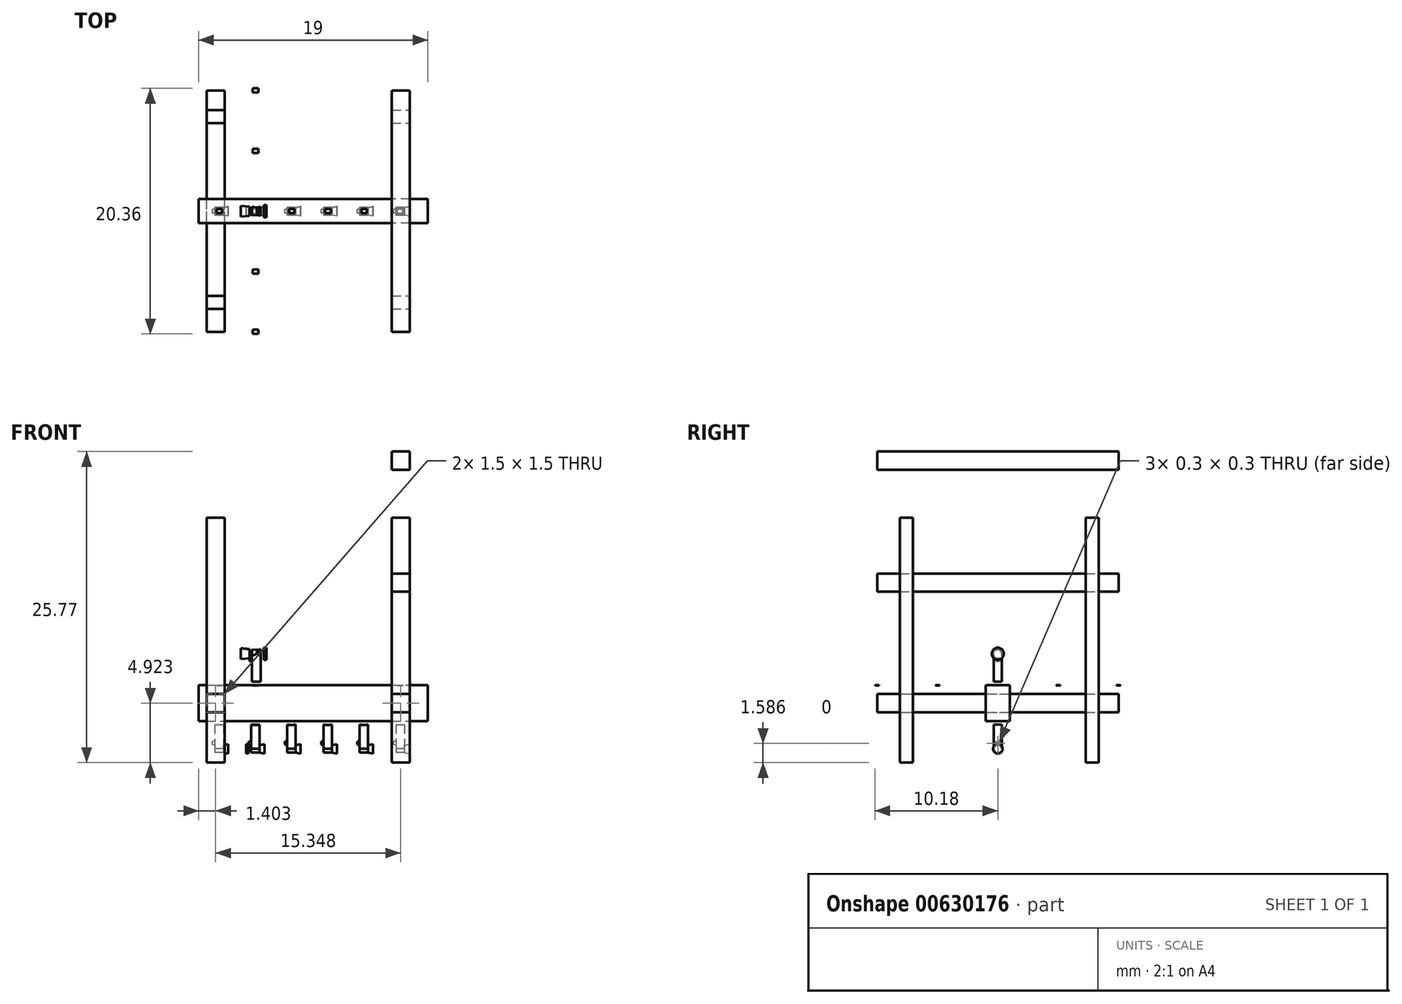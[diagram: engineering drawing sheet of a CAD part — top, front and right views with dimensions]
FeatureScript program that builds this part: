
annotation { "Feature Type Name" : "Feature", "Feature Type Description" : "" }
export const myFeature = defineFeature(function(context is Context, id is Id, definition is map)
    precondition{}
    {
        {
            var Q0;
            Q0=qCreatedBy(makeId("Front.planeOp"),FACE);
            var sketch = newSketch(context, id + "F0", { "sketchPlane" : qUnion([Q0])});
            skLineSegment(sketch, "E0.bottom", {"start": v(-0.48, 0) * mm, "end": v(0.22, 0) * mm});
            skLineSegment(sketch, "E0.top", {"start": v(-0.48, -2) * mm, "end": v(0.22, -2) * mm});
            skLineSegment(sketch, "E0.left", {"start": v(-0.48, 0) * mm, "end": v(-0.48, -2) * mm});
            skLineSegment(sketch, "E0.right", {"start": v(0.22, 0) * mm, "end": v(0.22, -2) * mm});
            skLineSegment(sketch, "E1.bottom", {"start": v(-0.48, 0) * mm, "end": v(-0.68, 0) * mm});
            skLineSegment(sketch, "E1.top", {"start": v(-0.48, -0.3) * mm, "end": v(-0.68, -0.3) * mm});
            skLineSegment(sketch, "E1.left", {"start": v(-0.48, 0) * mm, "end": v(-0.48, -0.3) * mm});
            skLineSegment(sketch, "E1.right", {"start": v(-0.68, 0) * mm, "end": v(-0.68, -0.3) * mm});
            skLineSegment(sketch, "E2", {"start": v(-0.1, 0) * mm, "end": v(-1.4, -0.13) * mm});
            skLineSegment(sketch, "E3", {"start": v(-1.4, -0.13) * mm, "end": v(-1.4, 0.32) * mm});
            skLineSegment(sketch, "E4", {"start": v(-1.4, 0.32) * mm, "end": v(0, 0.32) * mm});
            skLineSegment(sketch, "E5", {"start": v(0, 0.32) * mm, "end": v(0, 0) * mm});
            skLineSegment(sketch, "E6", {"start": v(0, 0) * mm, "end": v(0.5, -0.13) * mm});
            skLineSegment(sketch, "E7", {"start": v(0.5, -0.13) * mm, "end": v(0.5, 0.32) * mm});
            skLineSegment(sketch, "E8", {"start": v(0, 0.32) * mm, "end": v(0.5, 0.32) * mm});
            skLineSegment(sketch, "E9.bottom", {"start": v(0.5, 0.32) * mm, "end": v(0.7, 0.32) * mm});
            skLineSegment(sketch, "E9.top", {"start": v(0.5, -0.18) * mm, "end": v(0.7, -0.18) * mm});
            skLineSegment(sketch, "E9.left", {"start": v(0.5, 0.32) * mm, "end": v(0.5, -0.18) * mm});
            skLineSegment(sketch, "E9.right", {"start": v(0.7, 0.32) * mm, "end": v(0.7, -0.18) * mm});
            skLineSegment(sketch, "E10.bottom", {"start": v(-0.42, -2) * mm, "end": v(0.03, -2) * mm});
            skLineSegment(sketch, "E10.top", {"start": v(-0.42, -2.3) * mm, "end": v(0.03, -2.3) * mm});
            skLineSegment(sketch, "E10.left", {"start": v(-0.42, -2) * mm, "end": v(-0.42, -2.3) * mm});
            skLineSegment(sketch, "E10.right", {"start": v(0.03, -2) * mm, "end": v(0.03, -2.3) * mm});
            skLineSegment(sketch, "E11.top", {"start": v(-0.48, 0.32) * mm, "end": v(0.22, 0.32) * mm});
            skLineSegment(sketch, "E11.left", {"start": v(-0.48, 0) * mm, "end": v(-0.48, 0.32) * mm});
            skLineSegment(sketch, "E11.right", {"start": v(0.22, 0) * mm, "end": v(0.22, 0.32) * mm});
            skLineSegment(sketch, "E12.bottom", {"start": v(-0.68, 0) * mm, "end": v(-0.48, 0) * mm});
            skLineSegment(sketch, "E12.top", {"start": v(-0.68, 0.32) * mm, "end": v(-0.48, 0.32) * mm});
            skLineSegment(sketch, "E12.left", {"start": v(-0.68, 0) * mm, "end": v(-0.68, 0.32) * mm});
            skLineSegment(sketch, "E13.bottom", {"start": v(-4.9, -2.28) * mm, "end": v(14.1, -2.28) * mm});
            skLineSegment(sketch, "E13.top", {"start": v(-4.9, -5.28) * mm, "end": v(14.1, -5.28) * mm});
            skLineSegment(sketch, "E13.left", {"start": v(-4.9, -2.28) * mm, "end": v(-4.9, -5.28) * mm});
            skLineSegment(sketch, "E13.right", {"start": v(14.1, -2.28) * mm, "end": v(14.1, -5.28) * mm});
            skLineSegment(sketch, "E14.bottom", {"start": v(0, -5.28) * mm, "end": v(-0.45, -5.28) * mm});
            skLineSegment(sketch, "E14.top", {"start": v(0, -5.58) * mm, "end": v(-0.45, -5.58) * mm});
            skLineSegment(sketch, "E14.left", {"start": v(0, -5.28) * mm, "end": v(0, -5.58) * mm});
            skLineSegment(sketch, "E14.right", {"start": v(-0.45, -5.28) * mm, "end": v(-0.45, -5.58) * mm});
            skLineSegment(sketch, "E15.bottom", {"start": v(-0.56, -5.56) * mm, "end": v(0.14, -5.56) * mm});
            skLineSegment(sketch, "E15.top", {"start": v(-0.56, -7.56) * mm, "end": v(0.14, -7.56) * mm});
            skLineSegment(sketch, "E15.left", {"start": v(-0.56, -5.56) * mm, "end": v(-0.56, -7.56) * mm});
            skLineSegment(sketch, "E15.right", {"start": v(0.14, -5.56) * mm, "end": v(0.14, -7.56) * mm});
            skLineSegment(sketch, "E16", {"start": v(0.14, -7.56) * mm, "end": v(0.54, -7.56) * mm});
            skLineSegment(sketch, "E17", {"start": v(0.54, -7.56) * mm, "end": v(0.54, -7.16) * mm});
            skLineSegment(sketch, "E18", {"start": v(0.54, -7.16) * mm, "end": v(0.14, -7.26) * mm});
            skLineSegment(sketch, "E19", {"start": v(0.14, -7.26) * mm, "end": v(0.14, -7.56) * mm});
            skLineSegment(sketch, "E20", {"start": v(0.14, -7.26) * mm, "end": v(-0.56, -7.26) * mm});
            skLineSegment(sketch, "E21", {"start": v(-0.56, -7.26) * mm, "end": v(-0.96, -7.16) * mm});
            skLineSegment(sketch, "E22", {"start": v(-0.96, -7.56) * mm, "end": v(-0.96, -7.16) * mm});
            skLineSegment(sketch, "E23", {"start": v(-0.96, -7.56) * mm, "end": v(-0.56, -7.56) * mm});
            skLineSegment(sketch, "E24.bottom", {"start": v(-0.56, -7.56) * mm, "end": v(-0.76, -7.56) * mm});
            skLineSegment(sketch, "E24.top", {"start": v(-0.56, -6.96) * mm, "end": v(-0.76, -6.96) * mm});
            skLineSegment(sketch, "E24.left", {"start": v(-0.56, -7.56) * mm, "end": v(-0.56, -6.96) * mm});
            skLineSegment(sketch, "E24.right", {"start": v(-0.76, -7.56) * mm, "end": v(-0.76, -6.96) * mm});
            skLineSegment(sketch, "E25.bottom", {"start": v(-4.26, -3.03) * mm, "end": v(-2.76, -3.03) * mm});
            skLineSegment(sketch, "E25.top", {"start": v(-4.26, -4.53) * mm, "end": v(-2.76, -4.53) * mm});
            skLineSegment(sketch, "E25.left", {"start": v(-4.26, -3.03) * mm, "end": v(-4.26, -4.53) * mm});
            skLineSegment(sketch, "E25.right", {"start": v(-2.76, -3.03) * mm, "end": v(-2.76, -4.53) * mm});
            skLineSegment(sketch, "E26.bottom", {"start": v(12.6, -3.03) * mm, "end": v(11.1, -3.03) * mm});
            skLineSegment(sketch, "E26.top", {"start": v(12.6, -4.53) * mm, "end": v(11.1, -4.53) * mm});
            skLineSegment(sketch, "E26.left", {"start": v(12.6, -3.03) * mm, "end": v(12.6, -4.53) * mm});
            skLineSegment(sketch, "E26.right", {"start": v(11.1, -3.03) * mm, "end": v(11.1, -4.53) * mm});
            skLineSegment(sketch, "E27", {"start": v(-4.26, -3.03) * mm, "end": v(-4.26, -2.28) * mm});
            skLineSegment(sketch, "E28", {"start": v(12.6, -3.03) * mm, "end": v(12.6, -2.28) * mm});
            skSolve(sketch);
        }
        {
            var Q0;
            Q0=makeQuery(id+"F0.imprint","IMPRINT",FACE,{"disambiguationData":[TD([[makeQuery(id+"F0.imprint","IMPRINT",EDGE,{"derivedFrom":sQuery(id+"F0.wireOp",EDGE,"E12.bottom")}),1.0]])]});
            var Q1;
            {var subQ0=sQuery(id+"F0.wireOp",EDGE,"E12.bottom");Q1=makeQuery(id+"F0.imprint","IMPRINT",FACE,{"disambiguationData":[TD([[makeQuery(id+"F0.imprint","IMPRINT",EDGE,{"derivedFrom":subQ0}),-1.0]])]});}
            var Q2;
            {var subQ0=sQuery(id+"F0.wireOp",EDGE,"E0.bottom");var subQ3=sQuery(id+"F0.wireOp",EDGE,"E2");var subQ5=makeQuery(id+"F0.imprint","INTERSECT",VERTEX,{"derivedFrom":[subQ3,subQ0]});Q2=makeQuery(id+"F0.imprint","IMPRINT",FACE,{"disambiguationData":[TD([[makeQuery(id+"F0.imprint","IMPRINT",EDGE,{"disambiguationData":[TD([[subQ5,-1.0]])],"derivedFrom":subQ3}),-1.0]])]});}
            var Q3;
            {var subQ1=sQuery(id+"F0.wireOp",EDGE,"E5");Q3=makeQuery(id+"F0.imprint","IMPRINT",FACE,{"disambiguationData":[TD([[makeQuery(id+"F0.imprint","IMPRINT",EDGE,{"derivedFrom":subQ1}),-1.0]])]});}
            var Q4;
            {var subQ0=sQuery(id+"F0.wireOp",EDGE,"E5");Q4=makeQuery(id+"F0.imprint","IMPRINT",FACE,{"disambiguationData":[TD([[makeQuery(id+"F0.imprint","IMPRINT",EDGE,{"derivedFrom":subQ0}),1.0]])]});}
            var Q5;
            {var subQ1=sQuery(id+"F0.wireOp",EDGE,"E0.right");var subQ3=sQuery(id+"F0.wireOp",EDGE,"E6");var subQ4=makeQuery(id+"F0.imprint","INTERSECT",VERTEX,{"derivedFrom":[subQ1,subQ3]});Q5=makeQuery(id+"F0.imprint","IMPRINT",FACE,{"disambiguationData":[TD([[makeQuery(id+"F0.imprint","IMPRINT",EDGE,{"disambiguationData":[TD([[subQ4,1.0]])],"derivedFrom":subQ1}),-1.0]])]});}
            var Q6;
            {var subQ3=sQuery(id+"F0.wireOp",EDGE,"E9.bottom");Q6=makeQuery(id+"F0.imprint","IMPRINT",FACE,{"disambiguationData":[TD([[makeQuery(id+"F0.imprint","IMPRINT",EDGE,{"derivedFrom":subQ3}),-1.0]])]});}
            var Q7;
            {var subQ3=sQuery(id+"F0.wireOp",EDGE,"E8");Q7=makeQuery(id+"F0.imprint","IMPRINT",FACE,{"disambiguationData":[TD([[makeQuery(id+"F0.imprint","IMPRINT",EDGE,{"derivedFrom":subQ3}),-1.0]])]});}
            var Q8;
            {var subQ1=sQuery(id+"F0.wireOp",EDGE,"E3");Q8=makeQuery(id+"F0.imprint","IMPRINT",FACE,{"disambiguationData":[TD([[makeQuery(id+"F0.imprint","IMPRINT",EDGE,{"derivedFrom":subQ1}),-1.0]])]});}
            var Q9;
            Q9=sQuery(id+"F0.wireOp",EDGE,"E4");
            revolve(context, id + "F1", {"entities" : qUnion([Q0, Q1, Q2, Q3, Q4, Q5, Q6, Q7, Q8]), "axis" : qUnion([Q9]), "revolveType" : RevolveType.FULL});
        }
        {
            var Q0;
            {var subQ0=sQuery(id+"F0.wireOp",EDGE,"E1.top");Q0=makeQuery(id+"F0.imprint","IMPRINT",FACE,{"disambiguationData":[TD([[makeQuery(id+"F0.imprint","IMPRINT",EDGE,{"derivedFrom":subQ0}),-1.0]])]});}
            var Q1;
            Q1=makeQuery(id+"F0.imprint","IMPRINT",FACE,{"disambiguationData":[TD([[makeQuery(id+"F0.imprint","IMPRINT",EDGE,{"derivedFrom":sQuery(id+"F0.wireOp",EDGE,"E12.bottom")}),1.0]])]});
            var Q2;
            {var subQ0=sQuery(id+"F0.wireOp",EDGE,"E12.bottom");Q2=makeQuery(id+"F0.imprint","IMPRINT",FACE,{"disambiguationData":[TD([[makeQuery(id+"F0.imprint","IMPRINT",EDGE,{"derivedFrom":subQ0}),-1.0]])]});}
            extrude(context, id + "F2", {"entities" : qUnion([Q0, Q1, Q2]), "operationType" : NewBodyOperationType.ADD, "depth" : 0.3 * mm, "offsetDistance" : 25 * mm, "symmetric" : true});
        }
        {
            var Q0;
            {var subQ5=sQuery(id+"F0.wireOp",EDGE,"E0.left");Q0=makeQuery(id+"F0.imprint","IMPRINT",FACE,{"disambiguationData":[TD([[makeQuery(id+"F0.imprint","IMPRINT",EDGE,{"derivedFrom":subQ5}),1.0]])]});}
            var Q1;
            {var subQ0=sQuery(id+"F0.wireOp",EDGE,"E0.bottom");var subQ3=sQuery(id+"F0.wireOp",EDGE,"E2");var subQ5=makeQuery(id+"F0.imprint","INTERSECT",VERTEX,{"derivedFrom":[subQ3,subQ0]});Q1=makeQuery(id+"F0.imprint","IMPRINT",FACE,{"disambiguationData":[TD([[makeQuery(id+"F0.imprint","IMPRINT",EDGE,{"disambiguationData":[TD([[subQ5,-1.0]])],"derivedFrom":subQ3}),-1.0]])]});}
            var Q2;
            {var subQ1=sQuery(id+"F0.wireOp",EDGE,"E0.right");var subQ3=sQuery(id+"F0.wireOp",EDGE,"E6");var subQ4=makeQuery(id+"F0.imprint","INTERSECT",VERTEX,{"derivedFrom":[subQ1,subQ3]});Q2=makeQuery(id+"F0.imprint","IMPRINT",FACE,{"disambiguationData":[TD([[makeQuery(id+"F0.imprint","IMPRINT",EDGE,{"disambiguationData":[TD([[subQ4,1.0]])],"derivedFrom":subQ1}),-1.0]])]});}
            var Q3;
            {var subQ1=sQuery(id+"F0.wireOp",EDGE,"E5");Q3=makeQuery(id+"F0.imprint","IMPRINT",FACE,{"disambiguationData":[TD([[makeQuery(id+"F0.imprint","IMPRINT",EDGE,{"derivedFrom":subQ1}),-1.0]])]});}
            var Q4;
            {var subQ0=sQuery(id+"F0.wireOp",EDGE,"E5");Q4=makeQuery(id+"F0.imprint","IMPRINT",FACE,{"disambiguationData":[TD([[makeQuery(id+"F0.imprint","IMPRINT",EDGE,{"derivedFrom":subQ0}),1.0]])]});}
            extrude(context, id + "F3", {"entities" : qUnion([Q0, Q1, Q2, Q3, Q4]), "operationType" : NewBodyOperationType.ADD, "depth" : 0.65 * mm, "offsetDistance" : 25 * mm, "symmetric" : true});
        }
        {
            var Q0;
            Q0=makeQuery(id+"F0.imprint","IMPRINT",FACE,{"disambiguationData":[TD([[makeQuery(id+"F0.imprint","IMPRINT",EDGE,{"derivedFrom":sQuery(id+"F0.wireOp",EDGE,"E16")}),1.0]])]});
            var Q1;
            {var subQ5=sQuery(id+"F0.wireOp",EDGE,"E24.bottom");Q1=makeQuery(id+"F0.imprint","IMPRINT",FACE,{"disambiguationData":[TD([[makeQuery(id+"F0.imprint","IMPRINT",EDGE,{"derivedFrom":subQ5}),-1.0]])]});}
            var Q2;
            {var subQ0=sQuery(id+"F0.wireOp",EDGE,"E22");Q2=makeQuery(id+"F0.imprint","IMPRINT",FACE,{"disambiguationData":[TD([[makeQuery(id+"F0.imprint","IMPRINT",EDGE,{"derivedFrom":subQ0}),-1.0]])]});}
            var Q3;
            {var subQ0=sQuery(id+"F0.wireOp",EDGE,"E15.top");Q3=makeQuery(id+"F0.imprint","IMPRINT",FACE,{"disambiguationData":[TD([[makeQuery(id+"F0.imprint","IMPRINT",EDGE,{"derivedFrom":subQ0}),1.0]])]});}
            var Q4;
            Q4=sQuery(id+"F0.wireOp",EDGE,"E16");
            revolve(context, id + "F4", {"entities" : qUnion([Q0, Q1, Q2, Q3]), "axis" : qUnion([Q4]), "revolveType" : RevolveType.FULL});
        }
        {
            var Q0;
            {var subQ1=sQuery(id+"F0.wireOp",EDGE,"E14.top");Q0=makeQuery(id+"F0.imprint","IMPRINT",FACE,{"disambiguationData":[TD([[makeQuery(id+"F0.imprint","IMPRINT",EDGE,{"derivedFrom":subQ1}),1.0]])]});}
            var Q1;
            {var subQ0=sQuery(id+"F0.wireOp",EDGE,"E15.top");Q1=makeQuery(id+"F0.imprint","IMPRINT",FACE,{"disambiguationData":[TD([[makeQuery(id+"F0.imprint","IMPRINT",EDGE,{"derivedFrom":subQ0}),1.0]])]});}
            extrude(context, id + "F5", {"entities" : qUnion([Q0, Q1]), "operationType" : NewBodyOperationType.ADD, "depth" : 0.65 * mm, "offsetDistance" : 25 * mm, "symmetric" : true});
        }
        {
            var Q0;
            {var subQ5=sQuery(id+"F0.wireOp",EDGE,"E24.top");Q0=makeQuery(id+"F0.imprint","IMPRINT",FACE,{"disambiguationData":[TD([[makeQuery(id+"F0.imprint","IMPRINT",EDGE,{"derivedFrom":subQ5}),1.0]])]});}
            var Q1;
            {var subQ5=sQuery(id+"F0.wireOp",EDGE,"E24.bottom");Q1=makeQuery(id+"F0.imprint","IMPRINT",FACE,{"disambiguationData":[TD([[makeQuery(id+"F0.imprint","IMPRINT",EDGE,{"derivedFrom":subQ5}),-1.0]])]});}
            extrude(context, id + "F6", {"entities" : qUnion([Q0, Q1]), "operationType" : NewBodyOperationType.ADD, "depth" : 0.3 * mm, "offsetDistance" : 25 * mm, "symmetric" : true});
        }
        {
            var Q0;
            {var subQ0=sQuery(id+"F0.wireOp",EDGE,"E14.bottom");Q0=makeQuery(id+"F0.imprint","IMPRINT",FACE,{"disambiguationData":[TD([[makeQuery(id+"F0.imprint","IMPRINT",EDGE,{"derivedFrom":subQ0}),1.0]])]});}
            var Q1;
            {var subQ0=sQuery(id+"F0.wireOp",EDGE,"E14.top");Q1=makeQuery(id+"F0.imprint","IMPRINT",FACE,{"disambiguationData":[TD([[makeQuery(id+"F0.imprint","IMPRINT",EDGE,{"derivedFrom":subQ0}),-1.0]])]});}
            extrude(context, id + "F7", {"entities" : qUnion([Q0, Q1]), "depth" : 0.35 * mm, "offsetDistance" : 25 * mm, "symmetric" : true});
        }
        {
            var Q0;
            {var subQ0=sQuery(id+"F0.wireOp",EDGE,"E10.bottom");Q0=makeQuery(id+"F0.imprint","IMPRINT",FACE,{"disambiguationData":[TD([[makeQuery(id+"F0.imprint","IMPRINT",EDGE,{"derivedFrom":subQ0}),-1.0]])]});}
            var Q1;
            {var subQ0=sQuery(id+"F0.wireOp",EDGE,"E10.top");Q1=makeQuery(id+"F0.imprint","IMPRINT",FACE,{"disambiguationData":[TD([[makeQuery(id+"F0.imprint","IMPRINT",EDGE,{"derivedFrom":subQ0}),1.0]])]});}
            extrude(context, id + "F8", {"entities" : qUnion([Q0, Q1]), "depth" : 0.35 * mm, "offsetDistance" : 25 * mm, "symmetric" : true});
        }
        {
            var Q0;
            {var subQ1=sQuery(id+"F0.wireOp",EDGE,"E10.top");Q0=makeQuery(id+"F0.imprint","IMPRINT",FACE,{"disambiguationData":[TD([[makeQuery(id+"F0.imprint","IMPRINT",EDGE,{"derivedFrom":subQ1}),-1.0]])]});}
            var Q1;
            {var subQ0=sQuery(id+"F0.wireOp",EDGE,"E10.top");Q1=makeQuery(id+"F0.imprint","IMPRINT",FACE,{"disambiguationData":[TD([[makeQuery(id+"F0.imprint","IMPRINT",EDGE,{"derivedFrom":subQ0}),1.0]])]});}
            extrude(context, id + "F9", {"entities" : qUnion([Q0, Q1]), "depth" : 2 * mm, "offsetDistance" : 25 * mm, "symmetric" : true});
        }
        {
            var Q0;
            Q0=makeQuery(id+"F4.opRevolve","SWEPT_BODY",BODY,{"disambiguationData":[OSD([sQuery(id+"F0.wireOp",EDGE,"E15.top"),sQuery(id+"F0.wireOp",EDGE,"E16"),sQuery(id+"F0.wireOp",EDGE,"E17"),sQuery(id+"F0.wireOp",EDGE,"E18"),sQuery(id+"F0.wireOp",EDGE,"E20"),sQuery(id+"F0.wireOp",EDGE,"E21"),sQuery(id+"F0.wireOp",EDGE,"E22"),sQuery(id+"F0.wireOp",EDGE,"E23"),sQuery(id+"F0.wireOp",EDGE,"E24.bottom")])]});
            transform(context, id + "F10", {"entities" : qUnion([Q0]), "transformType" : TransformType.TRANSLATION_3D, "dx" : 3 * mm, "dy" : 0 * mm, "dz" : 0 * mm, "makeCopy" : true});
        }
        {
            var Q0;
            Q0=makeQuery(id+"F4.opRevolve","SWEPT_BODY",BODY,{"disambiguationData":[OSD([sQuery(id+"F0.wireOp",EDGE,"E15.top"),sQuery(id+"F0.wireOp",EDGE,"E16"),sQuery(id+"F0.wireOp",EDGE,"E17"),sQuery(id+"F0.wireOp",EDGE,"E18"),sQuery(id+"F0.wireOp",EDGE,"E20"),sQuery(id+"F0.wireOp",EDGE,"E21"),sQuery(id+"F0.wireOp",EDGE,"E22"),sQuery(id+"F0.wireOp",EDGE,"E23"),sQuery(id+"F0.wireOp",EDGE,"E24.bottom")])]});
            transform(context, id + "F11", {"entities" : qUnion([Q0]), "transformType" : TransformType.TRANSLATION_3D, "dx" : -3 * mm, "dy" : 0 * mm, "dz" : 0 * mm, "makeCopy" : true});
        }
        {
            var Q0;
            Q0=makeQuery(id+"F8.opExtrude","SWEPT_BODY",BODY,{"disambiguationData":[OSD([sQuery(id+"F0.wireOp",EDGE,"E10.bottom"),sQuery(id+"F0.wireOp",EDGE,"E10.top"),sQuery(id+"F0.wireOp",EDGE,"E10.left"),sQuery(id+"F0.wireOp",EDGE,"E10.right")])]});
            transform(context, id + "F12", {"entities" : qUnion([Q0]), "transformType" : TransformType.TRANSLATION_3D, "dx" : 3 * mm, "dy" : 0 * mm, "dz" : 0 * mm, "makeCopy" : true});
        }
        {
            var Q0;
            Q0=makeQuery(id+"F8.opExtrude","SWEPT_BODY",BODY,{"disambiguationData":[OSD([sQuery(id+"F0.wireOp",EDGE,"E10.bottom"),sQuery(id+"F0.wireOp",EDGE,"E10.top"),sQuery(id+"F0.wireOp",EDGE,"E10.left"),sQuery(id+"F0.wireOp",EDGE,"E10.right")])]});
            transform(context, id + "F13", {"entities" : qUnion([Q0]), "transformType" : TransformType.TRANSLATION_3D, "dx" : -3 * mm, "dy" : 0 * mm, "dz" : 0 * mm, "makeCopy" : true});
        }
        {
            var Q0;
            Q0=makeQuery(id+"F4.opRevolve","SWEPT_BODY",BODY,{"disambiguationData":[OSD([sQuery(id+"F0.wireOp",EDGE,"E15.top"),sQuery(id+"F0.wireOp",EDGE,"E16"),sQuery(id+"F0.wireOp",EDGE,"E17"),sQuery(id+"F0.wireOp",EDGE,"E18"),sQuery(id+"F0.wireOp",EDGE,"E20"),sQuery(id+"F0.wireOp",EDGE,"E21"),sQuery(id+"F0.wireOp",EDGE,"E22"),sQuery(id+"F0.wireOp",EDGE,"E23"),sQuery(id+"F0.wireOp",EDGE,"E24.bottom")])]});
            transform(context, id + "F14", {"entities" : qUnion([Q0]), "transformType" : TransformType.TRANSLATION_3D, "dx" : 6 * mm, "dy" : 0 * mm, "dz" : 0 * mm, "makeCopy" : true});
        }
        {
            var Q0;
            Q0=makeQuery(id+"F4.opRevolve","SWEPT_BODY",BODY,{"disambiguationData":[OSD([sQuery(id+"F0.wireOp",EDGE,"E15.top"),sQuery(id+"F0.wireOp",EDGE,"E16"),sQuery(id+"F0.wireOp",EDGE,"E17"),sQuery(id+"F0.wireOp",EDGE,"E18"),sQuery(id+"F0.wireOp",EDGE,"E20"),sQuery(id+"F0.wireOp",EDGE,"E21"),sQuery(id+"F0.wireOp",EDGE,"E22"),sQuery(id+"F0.wireOp",EDGE,"E23"),sQuery(id+"F0.wireOp",EDGE,"E24.bottom")])]});
            transform(context, id + "F15", {"entities" : qUnion([Q0]), "transformType" : TransformType.TRANSLATION_3D, "dx" : 9 * mm, "dy" : 0 * mm, "dz" : 0 * mm, "makeCopy" : true});
        }
        {
            var Q0;
            Q0=makeQuery(id+"F4.opRevolve","SWEPT_BODY",BODY,{"disambiguationData":[OSD([sQuery(id+"F0.wireOp",EDGE,"E15.top"),sQuery(id+"F0.wireOp",EDGE,"E16"),sQuery(id+"F0.wireOp",EDGE,"E17"),sQuery(id+"F0.wireOp",EDGE,"E18"),sQuery(id+"F0.wireOp",EDGE,"E20"),sQuery(id+"F0.wireOp",EDGE,"E21"),sQuery(id+"F0.wireOp",EDGE,"E22"),sQuery(id+"F0.wireOp",EDGE,"E23"),sQuery(id+"F0.wireOp",EDGE,"E24.bottom")])]});
            transform(context, id + "F16", {"entities" : qUnion([Q0]), "transformType" : TransformType.TRANSLATION_3D, "dx" : 12 * mm, "dy" : 0 * mm, "dz" : 0 * mm, "makeCopy" : true});
        }
        {
            var Q0;
            Q0=makeQuery(id+"F8.opExtrude","SWEPT_BODY",BODY,{"disambiguationData":[OSD([sQuery(id+"F0.wireOp",EDGE,"E10.bottom"),sQuery(id+"F0.wireOp",EDGE,"E10.top"),sQuery(id+"F0.wireOp",EDGE,"E10.left"),sQuery(id+"F0.wireOp",EDGE,"E10.right")])]});
            transform(context, id + "F17", {"entities" : qUnion([Q0]), "transformType" : TransformType.TRANSLATION_3D, "dx" : 6 * mm, "dy" : 0 * mm, "dz" : 0 * mm, "makeCopy" : true});
        }
        {
            var Q0;
            Q0=makeQuery(id+"F8.opExtrude","SWEPT_BODY",BODY,{"disambiguationData":[OSD([sQuery(id+"F0.wireOp",EDGE,"E10.bottom"),sQuery(id+"F0.wireOp",EDGE,"E10.top"),sQuery(id+"F0.wireOp",EDGE,"E10.left"),sQuery(id+"F0.wireOp",EDGE,"E10.right")])]});
            transform(context, id + "F18", {"entities" : qUnion([Q0]), "transformType" : TransformType.TRANSLATION_3D, "dx" : 12 * mm, "dy" : 0 * mm, "dz" : 0 * mm, "makeCopy" : true});
        }
        {
            var Q0;
            Q0=makeQuery(id+"F8.opExtrude","SWEPT_BODY",BODY,{"disambiguationData":[OSD([sQuery(id+"F0.wireOp",EDGE,"E10.bottom"),sQuery(id+"F0.wireOp",EDGE,"E10.top"),sQuery(id+"F0.wireOp",EDGE,"E10.left"),sQuery(id+"F0.wireOp",EDGE,"E10.right")])]});
            transform(context, id + "F19", {"entities" : qUnion([Q0]), "transformType" : TransformType.TRANSLATION_3D, "dx" : 9 * mm, "dy" : 0 * mm, "dz" : 0 * mm, "makeCopy" : true});
        }
        {
            var Q0;
            Q0=makeQuery(id+"F8.opExtrude","SWEPT_BODY",BODY,{"disambiguationData":[OSD([sQuery(id+"F0.wireOp",EDGE,"E10.bottom"),sQuery(id+"F0.wireOp",EDGE,"E10.top"),sQuery(id+"F0.wireOp",EDGE,"E10.left"),sQuery(id+"F0.wireOp",EDGE,"E10.right")])]});
            transform(context, id + "F20", {"entities" : qUnion([Q0]), "transformType" : TransformType.TRANSLATION_3D, "dx" : 0 * mm, "dy" : 5 * mm, "dz" : 0 * mm, "makeCopy" : true});
        }
        {
            var Q0;
            Q0=makeQuery(id+"F20.opPattern","COPY",BODY,{"derivedFrom":makeQuery(id+"F8.opExtrude","SWEPT_BODY",BODY,{"disambiguationData":[OSD([sQuery(id+"F0.wireOp",EDGE,"E10.bottom"),sQuery(id+"F0.wireOp",EDGE,"E10.top"),sQuery(id+"F0.wireOp",EDGE,"E10.left"),sQuery(id+"F0.wireOp",EDGE,"E10.right")])]}),"instanceName":"1"});
            var Q1;
            Q1=makeQuery(id+"F8.opExtrude","SWEPT_BODY",BODY,{"disambiguationData":[OSD([sQuery(id+"F0.wireOp",EDGE,"E10.bottom"),sQuery(id+"F0.wireOp",EDGE,"E10.top"),sQuery(id+"F0.wireOp",EDGE,"E10.left"),sQuery(id+"F0.wireOp",EDGE,"E10.right")])]});
            transform(context, id + "F21", {"entities" : qUnion([Q0, Q1]), "transformType" : TransformType.TRANSLATION_3D, "dx" : 0 * mm, "dy" : 5 * mm, "dz" : 0 * mm, "makeCopy" : true});
        }
        {
            var Q0;
            Q0=makeQuery(id+"F8.opExtrude","SWEPT_BODY",BODY,{"disambiguationData":[OSD([sQuery(id+"F0.wireOp",EDGE,"E10.bottom"),sQuery(id+"F0.wireOp",EDGE,"E10.top"),sQuery(id+"F0.wireOp",EDGE,"E10.left"),sQuery(id+"F0.wireOp",EDGE,"E10.right")])]});
            transform(context, id + "F22", {"entities" : qUnion([Q0]), "transformType" : TransformType.TRANSLATION_3D, "dx" : 0 * mm, "dy" : -5 * mm, "dz" : 0 * mm, "makeCopy" : true});
        }
        {
            var Q0;
            Q0=makeQuery(id+"F8.opExtrude","SWEPT_BODY",BODY,{"disambiguationData":[OSD([sQuery(id+"F0.wireOp",EDGE,"E10.bottom"),sQuery(id+"F0.wireOp",EDGE,"E10.top"),sQuery(id+"F0.wireOp",EDGE,"E10.left"),sQuery(id+"F0.wireOp",EDGE,"E10.right")])]});
            transform(context, id + "F23", {"entities" : qUnion([Q0]), "transformType" : TransformType.TRANSLATION_3D, "dx" : 0 * mm, "dy" : -10 * mm, "dz" : 0 * mm, "makeCopy" : true});
        }
        {
            var Q0;
            Q0=makeQuery(id+"F0.imprint","IMPRINT",FACE,{"disambiguationData":[TD([[makeQuery(id+"F0.imprint","IMPRINT",EDGE,{"derivedFrom":sQuery(id+"F0.wireOp",EDGE,"E25.bottom")}),-1.0]])]});
            var Q1;
            Q1=makeQuery(id+"F0.imprint","IMPRINT",FACE,{"disambiguationData":[TD([[makeQuery(id+"F0.imprint","IMPRINT",EDGE,{"derivedFrom":sQuery(id+"F0.wireOp",EDGE,"E26.bottom")}),1.0]])]});
            extrude(context, id + "F24", {"entities" : qUnion([Q0, Q1]), "depth" : 20 * mm, "offsetDistance" : 25 * mm, "symmetric" : true});
        }
        {
            var Q0;
            Q0=makeQuery(id+"F24.opExtrude","SWEPT_BODY",BODY,{"disambiguationData":[OSD([sQuery(id+"F0.wireOp",EDGE,"E26.bottom"),sQuery(id+"F0.wireOp",EDGE,"E26.top"),sQuery(id+"F0.wireOp",EDGE,"E26.left"),sQuery(id+"F0.wireOp",EDGE,"E26.right")])]});
            transform(context, id + "F25", {"entities" : qUnion([Q0]), "transformType" : TransformType.TRANSLATION_3D, "dx" : 0 * mm, "dy" : 0 * mm, "dz" : 10 * mm, "makeCopy" : true});
        }
        {
            var Q0;
            Q0=qCreatedBy(makeId("Top.planeOp"),FACE);
            var sketch = newSketch(context, id + "F26", { "sketchPlane" : qUnion([Q0])});
            skLineSegment(sketch, "E29.bottom", {"start": v(-4.25, -7.04) * mm, "end": v(-2.76, -7.04) * mm});
            skLineSegment(sketch, "E29.top", {"start": v(-4.25, -8.11) * mm, "end": v(-2.76, -8.11) * mm});
            skLineSegment(sketch, "E29.left", {"start": v(-4.25, -7.04) * mm, "end": v(-4.25, -8.11) * mm});
            skLineSegment(sketch, "E29.right", {"start": v(-2.76, -7.04) * mm, "end": v(-2.76, -8.11) * mm});
            skSolve(sketch);
        }
        {
            var Q0;
            Q0=makeQuery(id+"F26.imprint","IMPRINT",FACE,{"disambiguationData":[TD([[makeQuery(id+"F26.imprint","IMPRINT",EDGE,{"derivedFrom":sQuery(id+"F26.wireOp",EDGE,"E29.bottom")}),-1.0]])]});
            extrude(context, id + "F27", {"entities" : qUnion([Q0]), "depth" : 11.6 * mm, "offsetDistance" : 25 * mm, "hasSecondDirection" : true, "secondDirectionOppositeDirection" : true, "secondDirectionDepth" : 8.7 * mm});
        }
        {
            var Q0;
            Q0=makeQuery(id+"F27.opExtrude","SWEPT_BODY",BODY,{"disambiguationData":[OSD([sQuery(id+"F26.wireOp",EDGE,"E29.bottom"),sQuery(id+"F26.wireOp",EDGE,"E29.top"),sQuery(id+"F26.wireOp",EDGE,"E29.left"),sQuery(id+"F26.wireOp",EDGE,"E29.right")])]});
            transform(context, id + "F28", {"entities" : qUnion([Q0]), "transformType" : TransformType.TRANSLATION_3D, "dx" : 0 * mm, "dy" : 15.4 * mm, "dz" : 0 * mm, "makeCopy" : true});
        }
        {
            var Q0;
            Q0=makeQuery(id+"F28.opPattern","COPY",BODY,{"derivedFrom":makeQuery(id+"F27.opExtrude","SWEPT_BODY",BODY,{"disambiguationData":[OSD([sQuery(id+"F26.wireOp",EDGE,"E29.bottom"),sQuery(id+"F26.wireOp",EDGE,"E29.top"),sQuery(id+"F26.wireOp",EDGE,"E29.left"),sQuery(id+"F26.wireOp",EDGE,"E29.right")])]}),"instanceName":"1"});
            transform(context, id + "F29", {"entities" : qUnion([Q0]), "transformType" : TransformType.TRANSLATION_3D, "dx" : 0 * mm, "dy" : 0 * mm, "dz" : 9 * mm, "makeCopy" : true});
        }
        {
            var Q0;
            Q0=makeQuery(id+"F28.opPattern","COPY",BODY,{"derivedFrom":makeQuery(id+"F27.opExtrude","SWEPT_BODY",BODY,{"disambiguationData":[OSD([sQuery(id+"F26.wireOp",EDGE,"E29.bottom"),sQuery(id+"F26.wireOp",EDGE,"E29.top"),sQuery(id+"F26.wireOp",EDGE,"E29.left"),sQuery(id+"F26.wireOp",EDGE,"E29.right")])]}),"instanceName":"1"});
            transform(context, id + "F30", {"entities" : qUnion([Q0]), "transformType" : TransformType.TRANSLATION_3D, "dx" : 15.35 * mm, "dy" : 0 * mm, "dz" : 0 * mm, "makeCopy" : true});
        }
        {
            var Q0;
            Q0=makeQuery(id+"F27.opExtrude","SWEPT_BODY",BODY,{"disambiguationData":[OSD([sQuery(id+"F26.wireOp",EDGE,"E29.bottom"),sQuery(id+"F26.wireOp",EDGE,"E29.top"),sQuery(id+"F26.wireOp",EDGE,"E29.left"),sQuery(id+"F26.wireOp",EDGE,"E29.right")])]});
            transform(context, id + "F31", {"entities" : qUnion([Q0]), "transformType" : TransformType.TRANSLATION_3D, "dx" : 15.35 * mm, "dy" : 0 * mm, "dz" : 0 * mm, "makeCopy" : true});
        }
        {
            var Q0;
            Q0=makeQuery(id+"F29.opPattern","COPY",BODY,{"derivedFrom":makeQuery(id+"F28.opPattern","COPY",BODY,{"derivedFrom":makeQuery(id+"F27.opExtrude","SWEPT_BODY",BODY,{"disambiguationData":[OSD([sQuery(id+"F26.wireOp",EDGE,"E29.bottom"),sQuery(id+"F26.wireOp",EDGE,"E29.top"),sQuery(id+"F26.wireOp",EDGE,"E29.left"),sQuery(id+"F26.wireOp",EDGE,"E29.right")])]}),"instanceName":"1"}),"instanceName":"1"});
            deleteBodies(context, id + "F32", {"entities" : qUnion([Q0])});
        }
        {
            var Q0;
            Q0=makeQuery(id+"F24.opExtrude","SWEPT_BODY",BODY,{"disambiguationData":[OSD([sQuery(id+"F0.wireOp",EDGE,"E26.bottom"),sQuery(id+"F0.wireOp",EDGE,"E26.top"),sQuery(id+"F0.wireOp",EDGE,"E26.left"),sQuery(id+"F0.wireOp",EDGE,"E26.right")])]});
            transform(context, id + "F33", {"entities" : qUnion([Q0]), "transformType" : TransformType.TRANSLATION_3D, "dx" : 0 * mm, "dy" : 0 * mm, "dz" : 20.1 * mm, "makeCopy" : true});
        }
    });
